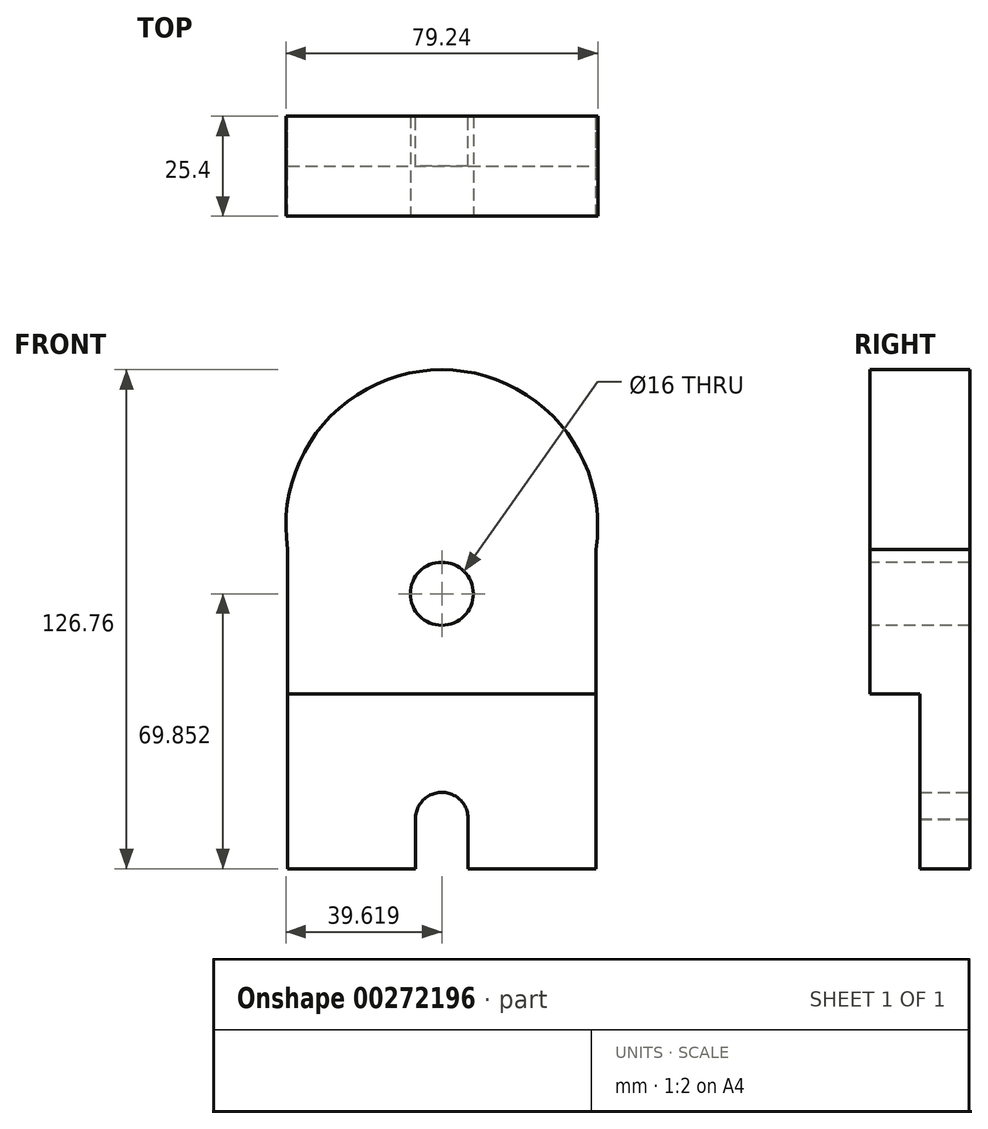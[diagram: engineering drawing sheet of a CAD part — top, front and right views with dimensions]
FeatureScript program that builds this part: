
annotation { "Feature Type Name" : "Feature", "Feature Type Description" : "" }
export const myFeature = defineFeature(function(context is Context, id is Id, definition is map)
    precondition{}
    {
        {
            var Q0;
            Q0=qCreatedBy(makeId("Front.planeOp"),FACE);
            var sketch = newSketch(context, id + "F0", { "sketchPlane" : qUnion([Q0])});
            skLineSegment(sketch, "E0", {"start": v(-47.36, -19.04) * mm, "end": v(-47.36, -55.87) * mm});
            skLineSegment(sketch, "E1", {"start": v(-47.36, -55.87) * mm, "end": v(-14.88, -55.87) * mm});
            skLineSegment(sketch, "E2", {"start": v(30.96, -55.87) * mm, "end": v(30.96, 25.23) * mm});
            skLineSegment(sketch, "E3", {"start": v(-47.36, -19.04) * mm, "end": v(-47.36, 25.23) * mm});
            skArc(sketch, "E4", {"start": v(30.96, 25.23) * mm, "mid": v(-8.2, 70.9) * mm, "end": v(-47.36, 25.23) * mm});
            skPoint(sketch, "E5.end.orphan", {"position": v(4.02, -38.53) * mm});
            skPoint(sketch, "E6.end.orphan", {"position": v(-8.2, -38.53) * mm});
            skPoint(sketch, "E6.start.orphan", {"position": v(-8.2, -55.87) * mm});
            skArc(sketch, "E7", {"start": v(-1.52, -43.37) * mm, "mid": v(-8.14, -36.5) * mm, "end": v(-14.88, -43.25) * mm});
            skLineSegment(sketch, "E8", {"start": v(-14.88, -43.1) * mm, "end": v(-14.88, -55.87) * mm});
            skLineSegment(sketch, "E9", {"start": v(-1.52, -42.99) * mm, "end": v(-1.52, -55.87) * mm});
            skLineSegment(sketch, "E10.trimOffspring", {"start": v(-1.52, -55.87) * mm, "end": v(30.96, -55.87) * mm});
            skSolve(sketch);
        }
        {
            var Q0;
            Q0=makeQuery(id+"F0.imprint","IMPRINT",FACE,{"disambiguationData":[TD([[makeQuery(id+"F0.imprint","IMPRINT",EDGE,{"derivedFrom":sQuery(id+"F0.wireOp",EDGE,"E0")}),1.0]])]});
            extrude(context, id + "F1", {"entities" : qUnion([Q0]), "depth" : 12.7 * mm});
        }
        {
            var Q0;
            Q0=makeQuery(id+"F1.opExtrude","CAP_FACE",FACE,{"disambiguationData":[OSD([sQuery(id+"F0.wireOp",EDGE,"E0"),sQuery(id+"F0.wireOp",EDGE,"E1"),sQuery(id+"F0.wireOp",EDGE,"E2"),sQuery(id+"F0.wireOp",EDGE,"E3"),sQuery(id+"F0.wireOp",EDGE,"E4"),sQuery(id+"F0.wireOp",EDGE,"E7"),sQuery(id+"F0.wireOp",EDGE,"E8"),sQuery(id+"F0.wireOp",EDGE,"E9"),sQuery(id+"F0.wireOp",EDGE,"E10.trimOffspring")])],"isStart":false});
            var sketch = newSketch(context, id + "F2", { "sketchPlane" : qUnion([Q0])});
            skLineSegment(sketch, "E11", {"start": v(-47.36, -55.87) * mm, "end": v(-47.36, -11.42) * mm});
            skLineSegment(sketch, "E12", {"start": v(-47.36, -11.42) * mm, "end": v(30.96, -11.42) * mm});
            skSolve(sketch);
        }
        {
            var Q0;
            {var subQ0=sQuery(id+"F2.wireOp",EDGE,"E12");Q0=makeQuery(id+"F2.imprint","IMPRINT",FACE,{"disambiguationData":[TD([[makeQuery(id+"F2.imprint","IMPRINT",EDGE,{"derivedFrom":subQ0}),1.0]])]});}
            extrude(context, id + "F3", {"entities" : qUnion([Q0]), "operationType" : NewBodyOperationType.ADD, "depth" : 12.7 * mm});
        }
        {
            var Q0;
            Q0=makeQuery(id+"F3.opExtrude","CAP_FACE",FACE,{"disambiguationData":[OSD([sQuery(id+"F0.wireOp",EDGE,"E0"),sQuery(id+"F0.wireOp",EDGE,"E2"),sQuery(id+"F0.wireOp",EDGE,"E3"),sQuery(id+"F0.wireOp",EDGE,"E4"),sQuery(id+"F2.wireOp",EDGE,"E12")])],"isStart":false});
            var sketch = newSketch(context, id + "F4", { "sketchPlane" : qUnion([Q0])});
            skLineSegment(sketch, "E13", {"start": v(-47.36, -11.42) * mm, "end": v(-47.36, 13.98) * mm});
            skLineSegment(sketch, "E14", {"start": v(-47.36, 13.98) * mm, "end": v(30.96, 13.98) * mm});
            skLineSegment(sketch, "E15", {"start": v(-8.2, 13.98) * mm, "end": v(-8.2, -11.42) * mm});
            skSolve(sketch);
        }
        {
            var Q0;
            Q0=sQuery(id+"F4.wireOp",VERTEX,"E15.start");
            var Q1;
            Q1=makeQuery(id+"F1.opExtrude","SWEPT_BODY",BODY,{"disambiguationData":[OSD([sQuery(id+"F0.wireOp",EDGE,"E0"),sQuery(id+"F0.wireOp",EDGE,"E1"),sQuery(id+"F0.wireOp",EDGE,"E2"),sQuery(id+"F0.wireOp",EDGE,"E3"),sQuery(id+"F0.wireOp",EDGE,"E4"),sQuery(id+"F0.wireOp",EDGE,"E7"),sQuery(id+"F0.wireOp",EDGE,"E8"),sQuery(id+"F0.wireOp",EDGE,"E9"),sQuery(id+"F0.wireOp",EDGE,"E10.trimOffspring")])]});
            hole(context, id + "F5", {"style" : HoleStyle.SIMPLE, "endStyle" : HoleEndStyle.THROUGH, "holeDiameter" : 16 * mm, "isTappedThrough" : true, "tappedDepth" : 12.7 * mm, "tapClearance" : 3, "locations" : qUnion([Q0]), "scope" : qUnion([Q1])});
        }
    });
